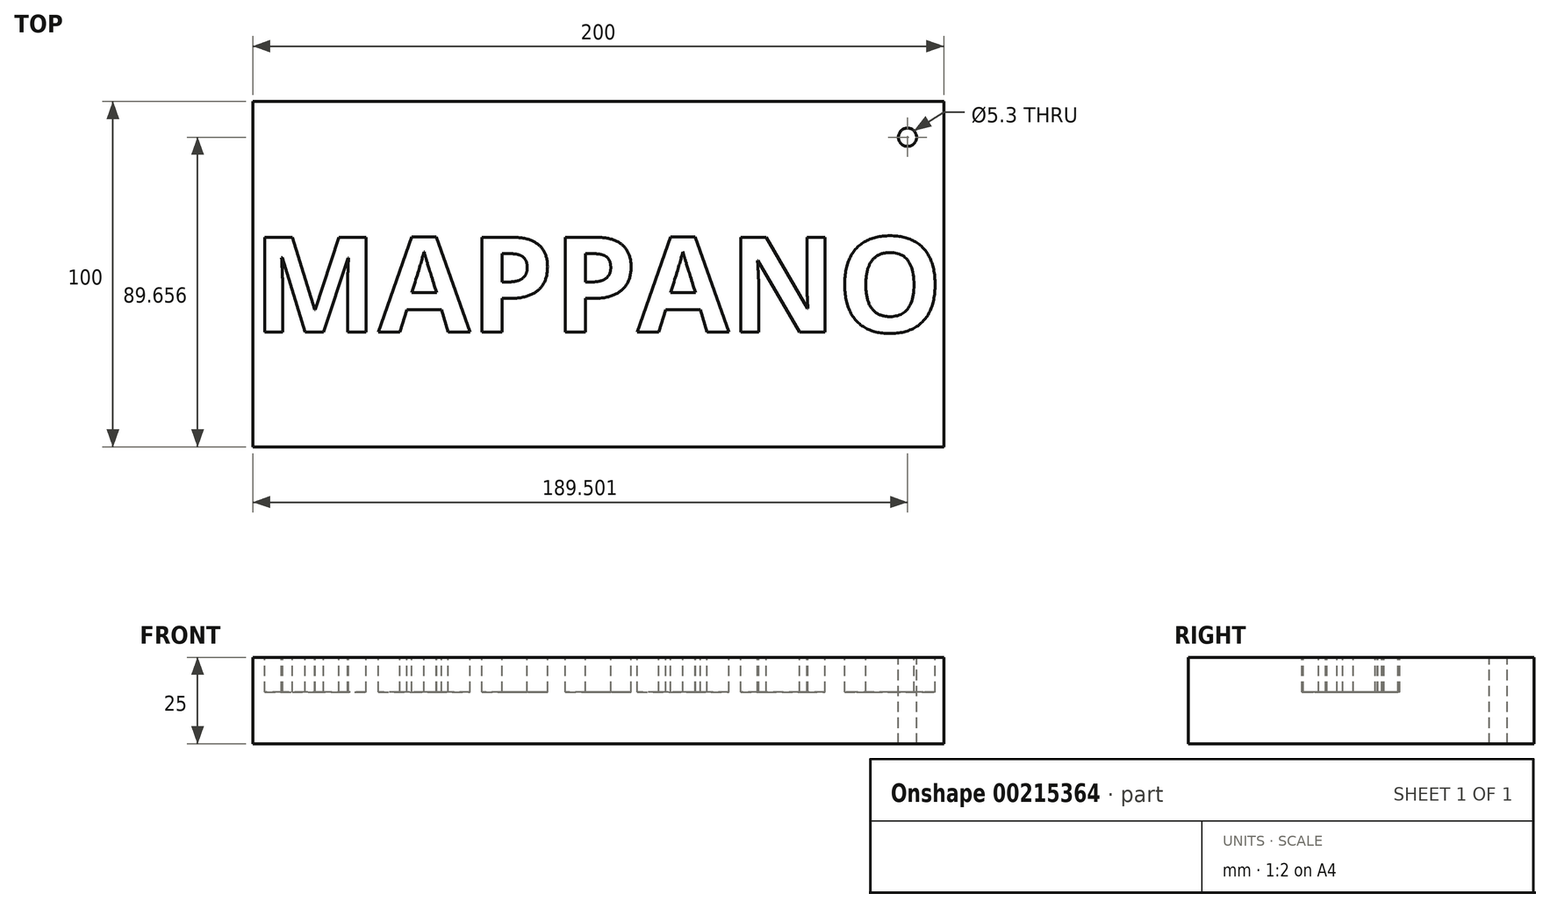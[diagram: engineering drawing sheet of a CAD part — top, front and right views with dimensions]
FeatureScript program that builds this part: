
annotation { "Feature Type Name" : "Feature", "Feature Type Description" : "" }
export const myFeature = defineFeature(function(context is Context, id is Id, definition is map)
    precondition{}
    {
        {
            var Q0;
            Q0=qCreatedBy(makeId("Top.planeOp"),FACE);
            var sketch = newSketch(context, id + "F0", { "sketchPlane" : qUnion([Q0])});
            skLineSegment(sketch, "E0.bottom", {"start": v(-100.09, 28.58) * mm, "end": v(99.91, 28.58) * mm});
            skLineSegment(sketch, "E0.top", {"start": v(-100.09, -71.42) * mm, "end": v(99.91, -71.42) * mm});
            skLineSegment(sketch, "E0.left", {"start": v(-100.09, 28.58) * mm, "end": v(-100.09, -71.42) * mm});
            skLineSegment(sketch, "E0.right", {"start": v(99.91, 28.58) * mm, "end": v(99.91, -71.42) * mm});
            skSolve(sketch);
        }
        {
            var Q0;
            Q0 = qSketchRegion(id + "F0", true);
            extrude(context, id + "F1", {"entities" : qUnion([Q0]), "oppositeDirection" : true, "depth" : 25 * mm, "offsetDistance" : 25 * mm});
        }
        {
            var Q0;
            Q0=makeQuery(id+"F1.opExtrude","CAP_FACE",FACE,{"disambiguationData":[OSD([sQuery(id+"F0.wireOp",EDGE,"E0.bottom"),sQuery(id+"F0.wireOp",EDGE,"E0.top"),sQuery(id+"F0.wireOp",EDGE,"E0.left"),sQuery(id+"F0.wireOp",EDGE,"E0.right")])],"isStart":true});
            var sketch = newSketch(context, id + "F2", { "sketchPlane" : qUnion([Q0])});
            skText(sketch, "E1", { "text": "MAPPANO", "fontName": "OpenSans-Bold.ttf"});
            const initialGuessF2  = {"E1": [-0.10009, -0.03822, 1, 0, 0.02772]};
            skSetInitialGuess(sketch, initialGuessF2);
            skSolve(sketch);
        }
        {
            var Q0;
            Q0 = qSketchRegion(id + "F2", true);
            extrude(context, id + "F3", {"entities" : qUnion([Q0]), "operationType" : NewBodyOperationType.REMOVE, "oppositeDirection" : true, "depth" : 10 * mm, "offsetDistance" : 25 * mm});
        }
        {
            var Q0;
            {var subQ0=sQuery(id+"F0.wireOp",EDGE,"E0.left");var subQ1=sQuery(id+"F0.wireOp",EDGE,"E0.bottom");var subQ2=sQuery(id+"F0.wireOp",EDGE,"E0.right");var subQ3=sQuery(id+"F0.wireOp",EDGE,"E0.top");Q0=makeQuery(id+"F3.boolean.opBoolean","SPLIT",FACE,{"disambiguationData":[TD([makeQuery(id+"F1.opExtrude","SWEPT_FACE",FACE,{"disambiguationData":[OSD([subQ1])]})])],"derivedFrom":makeQuery(id+"F1.opExtrude","CAP_FACE",FACE,{"disambiguationData":[OSD([subQ1,subQ3,subQ0,subQ2])],"isStart":true})});}
            var sketch = newSketch(context, id + "F4", { "sketchPlane" : qUnion([Q0])});
            skPoint(sketch, "E2", {"position": v(-88.97, 19.97) * mm});
            skPoint(sketch, "E3", {"position": v(89.41, 18.24) * mm});
            skSolve(sketch);
        }
        {
            var Q0;
            Q0=sQuery(id+"F4.wireOp",VERTEX,"E3");
            var Q1;
            Q1=makeQuery(id+"F1.opExtrude","SWEPT_BODY",BODY,{"disambiguationData":[OSD([sQuery(id+"F0.wireOp",EDGE,"E0.bottom"),sQuery(id+"F0.wireOp",EDGE,"E0.top"),sQuery(id+"F0.wireOp",EDGE,"E0.left"),sQuery(id+"F0.wireOp",EDGE,"E0.right")])]});
            hole(context, id + "F5", {"style" : HoleStyle.SIMPLE, "endStyle" : HoleEndStyle.THROUGH, "standardTappedOrClearance" : lookupTablePath({ "standard" : "ISO", "size" : "5.3", "type" : "Drilled" }), "standardBlindInLast" : lookupTablePath({ "standard" : "ISO", "size" : "5.3", "type" : "Drilled" }), "holeDiameter" : 5.3 * mm, "majorDiameter" : 5 * mm, "isTappedThrough" : true, "tappedDepth" : 12 * mm, "tapClearance" : 3, "startFromSketch" : true, "locations" : qUnion([Q0]), "scope" : qUnion([Q1])});
        }
    });
